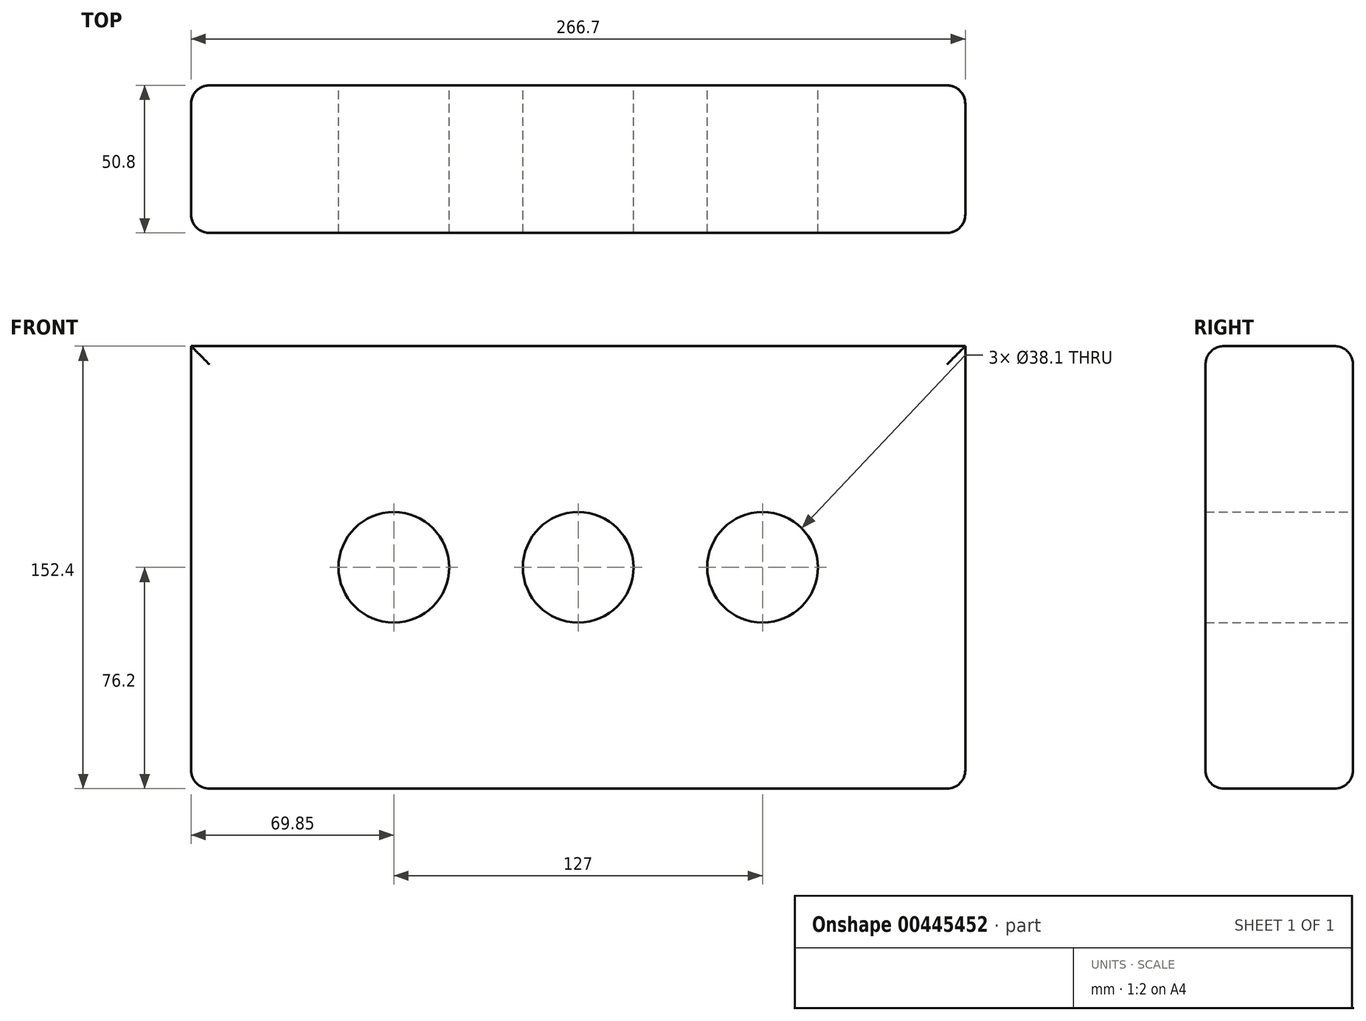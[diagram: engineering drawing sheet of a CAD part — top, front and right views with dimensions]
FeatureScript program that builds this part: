
annotation { "Feature Type Name" : "Feature", "Feature Type Description" : "" }
export const myFeature = defineFeature(function(context is Context, id is Id, definition is map)
    precondition{}
    {
        {
            var Q0;
            Q0=qCreatedBy(makeId("Front.planeOp"),FACE);
            var sketch = newSketch(context, id + "F0", { "sketchPlane" : qUnion([Q0])});
            skLineSegment(sketch, "E0.bottom", {"start": v(-133.35, -76.2) * mm, "end": v(133.35, -76.2) * mm});
            skLineSegment(sketch, "E0.top", {"start": v(-133.35, 76.2) * mm, "end": v(133.35, 76.2) * mm});
            skLineSegment(sketch, "E0.left", {"start": v(-133.35, -76.2) * mm, "end": v(-133.35, 76.2) * mm});
            skLineSegment(sketch, "E0.right", {"start": v(133.35, -76.2) * mm, "end": v(133.35, 76.2) * mm});
            skPoint(sketch, "E0.middle", {"position": v(0, 0) * mm});
            skSolve(sketch);
        }
        {
            var Q0;
            Q0=makeQuery(id+"F0.imprint","IMPRINT",FACE,{"disambiguationData":[TD([[makeQuery(id+"F0.imprint","IMPRINT",EDGE,{"derivedFrom":sQuery(id+"F0.wireOp",EDGE,"E0.bottom")}),1.0]])]});
            extrude(context, id + "F1", {"entities" : qUnion([Q0]), "depth" : 50.8 * mm});
        }
        {
            var Q0;
            Q0=qCreatedBy(makeId("Front.planeOp"),FACE);
            var sketch = newSketch(context, id + "F2", { "sketchPlane" : qUnion([Q0])});
            skCircle(sketch, "E1", {"center": v(0, 0) * mm, "radius": 19.05 * mm});
            skSolve(sketch);
        }
        {
            var Q0;
            Q0 = qSketchRegion(id + "F2", true);
            extrude(context, id + "F3", {"entities" : qUnion([Q0]), "operationType" : NewBodyOperationType.REMOVE, "endBound" : BoundingType.THROUGH_ALL, "depth" : 25.4 * mm});
        }
        {
            var Q0;
            Q0=qCreatedBy(makeId("Front.planeOp"),FACE);
            var sketch = newSketch(context, id + "F4", { "sketchPlane" : qUnion([Q0])});
            skLineSegment(sketch, "E2", {"start": v(0, 0) * mm, "end": v(-63.5, 0) * mm});
            skLineSegment(sketch, "E3", {"start": v(0, 0) * mm, "end": v(63.5, 0) * mm});
            skCircle(sketch, "E4", {"center": v(-63.5, 0) * mm, "radius": 19.05 * mm});
            skCircle(sketch, "E5", {"center": v(63.5, 0) * mm, "radius": 19.05 * mm});
            skSolve(sketch);
        }
        {
            var Q0;
            Q0 = qSketchRegion(id + "F4", true);
            extrude(context, id + "F5", {"entities" : qUnion([Q0]), "operationType" : NewBodyOperationType.REMOVE, "endBound" : BoundingType.THROUGH_ALL, "depth" : 25.4 * mm});
        }
        {
            var Q0;
            Q0=makeQuery(id+"F1.opExtrude","CAP_EDGE",EDGE,{"disambiguationData":[OSD([sQuery(id+"F0.wireOp",EDGE,"E0.left")])],"isStart":false});
            var Q1;
            Q1=makeQuery(id+"F1.opExtrude","CAP_EDGE",EDGE,{"disambiguationData":[OSD([sQuery(id+"F0.wireOp",EDGE,"E0.bottom")])],"isStart":false});
            var Q2;
            Q2=makeQuery(id+"F1.opExtrude","CAP_EDGE",EDGE,{"disambiguationData":[OSD([sQuery(id+"F0.wireOp",EDGE,"E0.top")])],"isStart":false});
            var Q3;
            Q3=makeQuery(id+"F1.opExtrude","CAP_EDGE",EDGE,{"disambiguationData":[OSD([sQuery(id+"F0.wireOp",EDGE,"E0.right")])],"isStart":false});
            var Q4;
            Q4=makeQuery(id+"F1.opExtrude","SWEPT_EDGE",EDGE,{"disambiguationData":[OSD([sQuery(id+"F0.wireOp",EDGE,"E0.bottom"),sQuery(id+"F0.wireOp",EDGE,"E0.left")])]});
            var Q5;
            Q5=makeQuery(id+"F1.opExtrude","CAP_EDGE",EDGE,{"disambiguationData":[OSD([sQuery(id+"F0.wireOp",EDGE,"E0.bottom")])],"isStart":true});
            var Q6;
            Q6=makeQuery(id+"F1.opExtrude","CAP_EDGE",EDGE,{"disambiguationData":[OSD([sQuery(id+"F0.wireOp",EDGE,"E0.left")])],"isStart":true});
            var Q7;
            Q7=makeQuery(id+"F1.opExtrude","SWEPT_EDGE",EDGE,{"disambiguationData":[OSD([sQuery(id+"F0.wireOp",EDGE,"E0.bottom"),sQuery(id+"F0.wireOp",EDGE,"E0.right")])]});
            var Q8;
            Q8=makeQuery(id+"F1.opExtrude","CAP_EDGE",EDGE,{"disambiguationData":[OSD([sQuery(id+"F0.wireOp",EDGE,"E0.right")])],"isStart":true});
            var Q9;
            Q9=makeQuery(id+"F1.opExtrude","CAP_EDGE",EDGE,{"disambiguationData":[OSD([sQuery(id+"F0.wireOp",EDGE,"E0.top")])],"isStart":true});
            fillet(context, id + "F6", {"entities" : qUnion([Q0, Q1, Q2, Q3, Q4, Q5, Q6, Q7, Q8, Q9]), "radius" : 6.35 * mm, "tangentPropagation" : true, "allowEdgeOverflow" : false});
        }
    });
